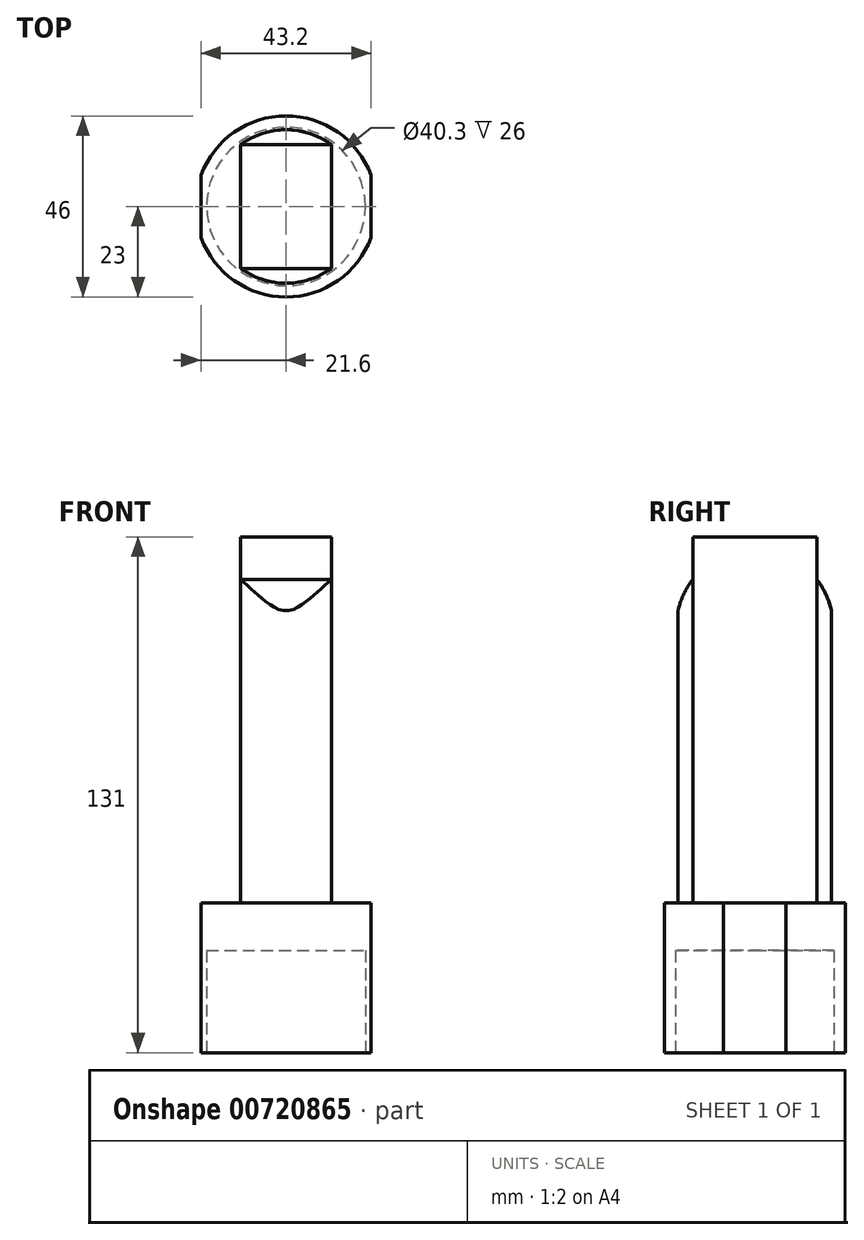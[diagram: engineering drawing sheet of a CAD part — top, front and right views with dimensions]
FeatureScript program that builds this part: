
annotation { "Feature Type Name" : "Feature", "Feature Type Description" : "" }
export const myFeature = defineFeature(function(context is Context, id is Id, definition is map)
    precondition{}
    {
        {
            var Q0;
            Q0=qCreatedBy(makeId("Top.planeOp"),FACE);
            var sketch = newSketch(context, id + "F0", { "sketchPlane" : qUnion([Q0])});
            skCircle(sketch, "E0", {"center": v(0, 0) * mm, "radius": 23 * mm});
            skPoint(sketch, "E1", {"position": v(-21.6, 0) * mm});
            skLineSegment(sketch, "E2", {"start": v(-21.6, -7.9) * mm, "end": v(-21.6, 7.9) * mm});
            skLineSegment(sketch, "E3.MirrorCS", {"start": v(21.6, -7.9) * mm, "end": v(21.6, 7.9) * mm});
            skSolve(sketch);
        }
        {
            var Q0;
            {var subQ0=sQuery(id+"F0.wireOp",EDGE,"E2");Q0=makeQuery(id+"F0.imprint","IMPRINT",FACE,{"disambiguationData":[TD([[makeQuery(id+"F0.imprint","IMPRINT",EDGE,{"derivedFrom":subQ0}),-1.0]])]});}
            extrude(context, id + "F1", {"entities" : qUnion([Q0]), "depth" : 38 * mm, "offsetDistance" : 25 * mm});
        }
        {
            var Q0;
            Q0=makeQuery(id+"F1.opExtrude","CAP_FACE",FACE,{"disambiguationData":[OSD([sQuery(id+"F0.wireOp",EDGE,"E0"),sQuery(id+"F0.wireOp",EDGE,"E2"),sQuery(id+"F0.wireOp",EDGE,"E3.MirrorCS")])],"isStart":false});
            var sketch = newSketch(context, id + "F2", { "sketchPlane" : qUnion([Q0])});
            skCircle(sketch, "E4", {"center": v(0, 0) * mm, "radius": 19.5 * mm});
            skPoint(sketch, "E5", {"position": v(11.5, 0) * mm});
            skLineSegment(sketch, "E6", {"start": v(11.5, 0) * mm, "end": v(11.5, -15.75) * mm});
            skLineSegment(sketch, "E7", {"start": v(11.5, -15.75) * mm, "end": v(11.5, 15.75) * mm});
            skLineSegment(sketch, "E8.MirrorCS", {"start": v(-11.5, -15.75) * mm, "end": v(-11.5, 15.75) * mm});
            skSolve(sketch);
        }
        {
            var Q0;
            {var subQ4=sQuery(id+"F2.wireOp",EDGE,"E8.MirrorCS");Q0=makeQuery(id+"F2.imprint","IMPRINT",FACE,{"disambiguationData":[TD([[makeQuery(id+"F2.imprint","IMPRINT",EDGE,{"derivedFrom":subQ4}),-1.0]])]});}
            extrude(context, id + "F3", {"entities" : qUnion([Q0]), "operationType" : NewBodyOperationType.ADD, "depth" : 93 * mm, "offsetDistance" : 25 * mm});
        }
        {
            var Q0;
            Q0=makeQuery(id+"F3.opExtrude","SWEPT_FACE",FACE,{"disambiguationData":[OSD([sQuery(id+"F2.wireOp",EDGE,"E7")])]});
            var sketch = newSketch(context, id + "F4", { "sketchPlane" : qUnion([Q0])});
            skCircle(sketch, "E9", {"center": v(0, 108) * mm, "radius": 19.96 * mm});
            skLineSegment(sketch, "E10", {"start": v(19.96, 108) * mm, "end": v(37.25, 135.03) * mm});
            skLineSegment(sketch, "E11", {"start": v(37.25, 135.03) * mm, "end": v(-38.25, 135.03) * mm});
            skLineSegment(sketch, "E12", {"start": v(-38.25, 135.03) * mm, "end": v(-19.96, 108) * mm});
            skSolve(sketch);
        }
        {
            var Q0;
            {var subQ0=sQuery(id+"F4.wireOp",EDGE,"E10");Q0=makeQuery(id+"F4.imprint","IMPRINT",FACE,{"disambiguationData":[TD([[makeQuery(id+"F4.imprint","IMPRINT",EDGE,{"derivedFrom":subQ0}),1.0]])]});}
            var Q1;
            {var subQ1=sQuery(id+"F2.wireOp",EDGE,"E7");var subQ7=makeQuery(id+"F3.opExtrude","CAP_EDGE",EDGE,{"disambiguationData":[OSD([subQ1])],"isStart":false});Q1=makeQuery(id+"F4.imprint","IMPRINT",FACE,{"disambiguationData":[TD([[makeQuery(id+"F4.imprint","IMPRINT",EDGE,{"derivedFrom":subQ7}),-1.0]])]});}
            extrude(context, id + "F5", {"entities" : qUnion([Q0, Q1]), "operationType" : NewBodyOperationType.REMOVE, "oppositeDirection" : true, "depth" : 35 * mm, "offsetDistance" : 25 * mm});
        }
        {
            var Q0;
            Q0=makeQuery(id+"F1.opExtrude","CAP_FACE",FACE,{"disambiguationData":[OSD([sQuery(id+"F0.wireOp",EDGE,"E0"),sQuery(id+"F0.wireOp",EDGE,"E2"),sQuery(id+"F0.wireOp",EDGE,"E3.MirrorCS")])],"isStart":true});
            var sketch = newSketch(context, id + "F6", { "sketchPlane" : qUnion([Q0])});
            skCircle(sketch, "E13", {"center": v(0, 0) * mm, "radius": 20.15 * mm});
            skSolve(sketch);
        }
        {
            var Q0;
            Q0 = qSketchRegion(id + "F6", true);
            extrude(context, id + "F7", {"entities" : qUnion([Q0]), "operationType" : NewBodyOperationType.REMOVE, "oppositeDirection" : true, "depth" : 26 * mm, "offsetDistance" : 25 * mm});
        }
    });
